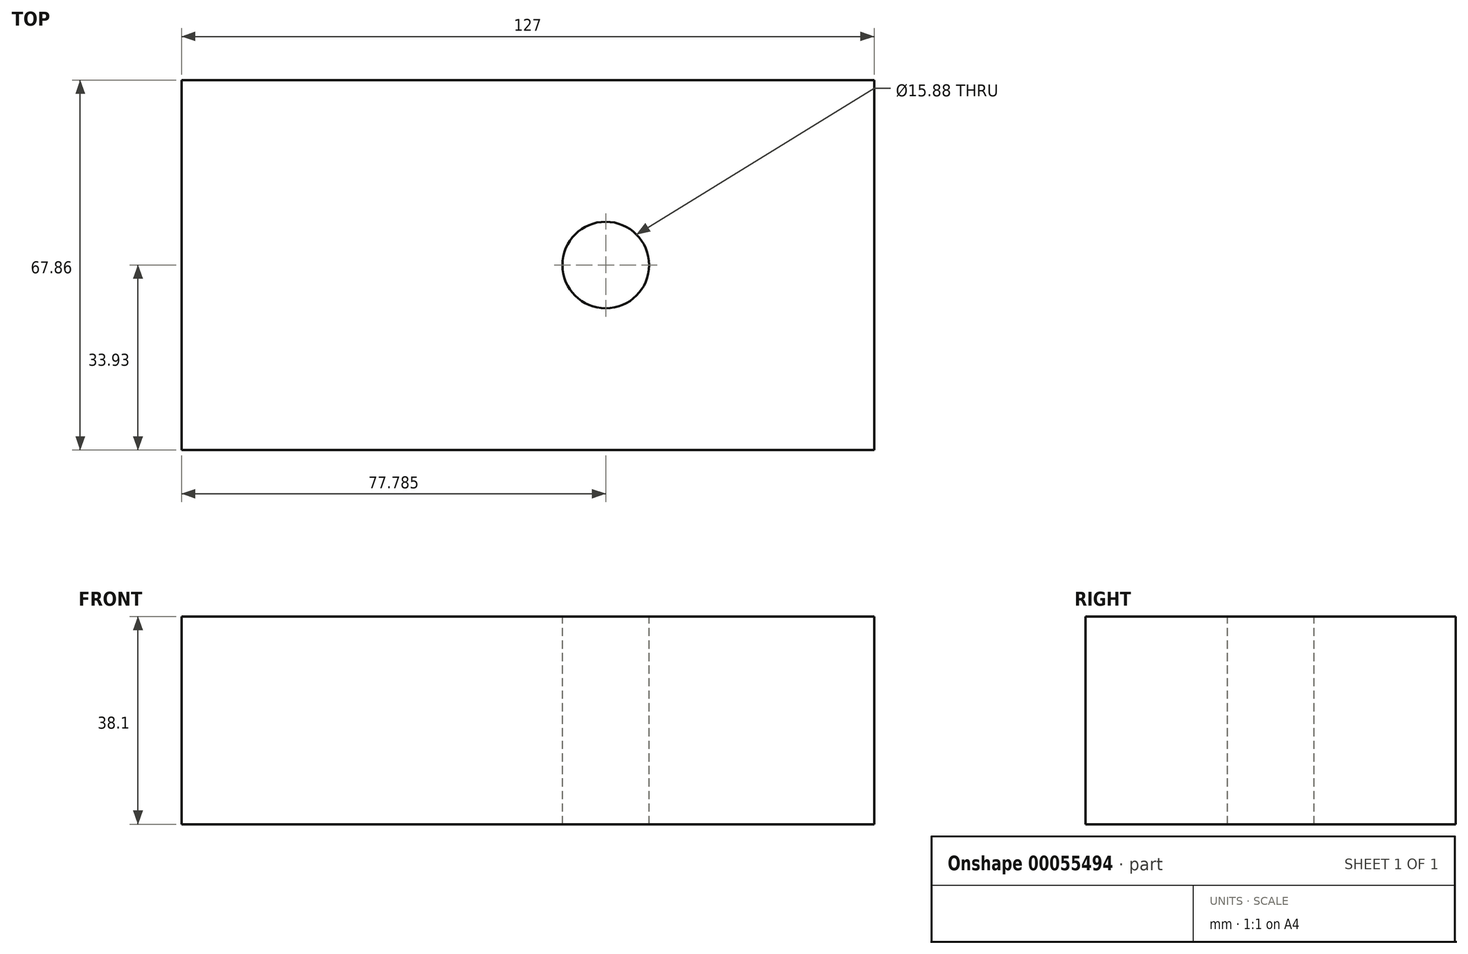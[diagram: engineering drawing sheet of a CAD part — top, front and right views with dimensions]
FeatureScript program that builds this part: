
annotation { "Feature Type Name" : "Feature", "Feature Type Description" : "" }
export const myFeature = defineFeature(function(context is Context, id is Id, definition is map)
    precondition{}
    {
        {
            var Q0;
            Q0=qCreatedBy(makeId("Top.planeOp"),FACE);
            var sketch = newSketch(context, id + "F0", { "sketchPlane" : qUnion([Q0])});
            skLineSegment(sketch, "E0.rect.bottom", {"start": v(-63.5, 33.93) * mm, "end": v(63.5, 33.93) * mm});
            skLineSegment(sketch, "E0.rect.top", {"start": v(-63.5, -33.93) * mm, "end": v(63.5, -33.93) * mm});
            skLineSegment(sketch, "E0.rect.left", {"start": v(-63.5, 33.93) * mm, "end": v(-63.5, -33.93) * mm});
            skLineSegment(sketch, "E0.rect.right", {"start": v(63.5, 33.93) * mm, "end": v(63.5, -33.93) * mm});
            skPoint(sketch, "E0.rect.middle", {"position": v(0, 0) * mm});
            skLineSegment(sketch, "E1", {"start": v(0, 0) * mm, "end": v(-14.28, 0) * mm});
            skCircle(sketch, "E2", {"center": v(-14.28, 0) * mm, "radius": 7.94 * mm});
            skCircle(sketch, "E3.MirrorC", {"center": v(14.28, 0) * mm, "radius": 7.94 * mm});
            skLineSegment(sketch, "E4.MirrorCS", {"start": v(0, 0) * mm, "end": v(14.28, 0) * mm});
            skSolve(sketch);
        }
        {
            var Q0;
            Q0=makeQuery(id+"F0.imprint","IMPRINT",FACE,{"disambiguationData":[TD([[makeQuery(id+"F0.imprint","IMPRINT",EDGE,{"derivedFrom":sQuery(id+"F0.wireOp",EDGE,"E0.rect.bottom")}),-1.0]])]});
            var Q1;
            Q1=makeQuery(id+"F0.imprint","IMPRINT",FACE,{"disambiguationData":[TD([[makeQuery(id+"F0.imprint","IMPRINT",EDGE,{"derivedFrom":sQuery(id+"F0.wireOp",EDGE,"E2")}),1.0]])]});
            var Q2;
            Q2=makeQuery(id+"F0.imprint","IMPRINT",FACE,{"disambiguationData":[TD([[makeQuery(id+"F0.imprint","IMPRINT",EDGE,{"derivedFrom":sQuery(id+"F0.wireOp",EDGE,"E3.MirrorC")}),-1.0]])]});
            extrude(context, id + "F1", {"entities" : qUnion([Q0, Q1, Q2]), "oppositeDirection" : true, "depth" : 25.4 * mm});
        }
        {
            var Q0;
            Q0=makeQuery(id+"F0.imprint","IMPRINT",FACE,{"disambiguationData":[TD([[makeQuery(id+"F0.imprint","IMPRINT",EDGE,{"derivedFrom":sQuery(id+"F0.wireOp",EDGE,"E2")}),1.0]])]});
            var Q1;
            Q1=makeQuery(id+"F0.imprint","IMPRINT",FACE,{"disambiguationData":[TD([[makeQuery(id+"F0.imprint","IMPRINT",EDGE,{"derivedFrom":sQuery(id+"F0.wireOp",EDGE,"E3.MirrorC")}),-1.0]])]});
            extrude(context, id + "F2", {"entities" : qUnion([Q0, Q1]), "operationType" : NewBodyOperationType.ADD, "depth" : 12.7 * mm});
        }
    });
